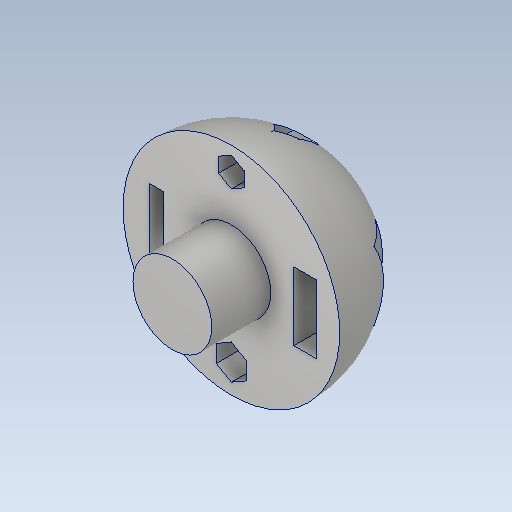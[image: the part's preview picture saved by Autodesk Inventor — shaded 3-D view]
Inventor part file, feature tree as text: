
AUTODESK INVENTOR PART (.ipt)
format: ipt  version: 2021 (Build 250183000, 183)  size: 173,056 bytes
history: native  units: in
note: dims shown in document units (in); Inventor stores cm internally (conversion verified against a paired STEP export)
features: sketch x4, extrude x3, revolve x1
ambient origin geometry x8: Origin, YZ Plane, XZ Plane, XY Plane, X Axis, Y Axis, Z Axis, Center Point
bodies: Solid1 (feature_tree)
feature tree (8):
  revolve  "Revolution1"  [1 undecoded]
  sketch  "Sketch2"  dims[d2=180.0deg d3=2.1654in d4=0.0in]
  extrude  "Extrusion1"  Depth=2.1654in TaperAngle=0.0deg
  extrude  "Extrusion2"  Depth=2.1654in
  extrude  "Extrusion4"  [1 undecoded]
  sketch  "Sketch1"  dims[d0=2.1654in d1=4.3307in]
  sketch  "Sketch3"  dims[d5=2.1654in d6=0.0in d9=1.5748in]
  sketch  "Sketch4"  dims[d10=1.1811in d11=0.0in]
note: 2 required parameter values undecoded (feature->parameter linkage not recoverable at this tier; creation-order binding heuristic only, values carry confidence <= 0.55)